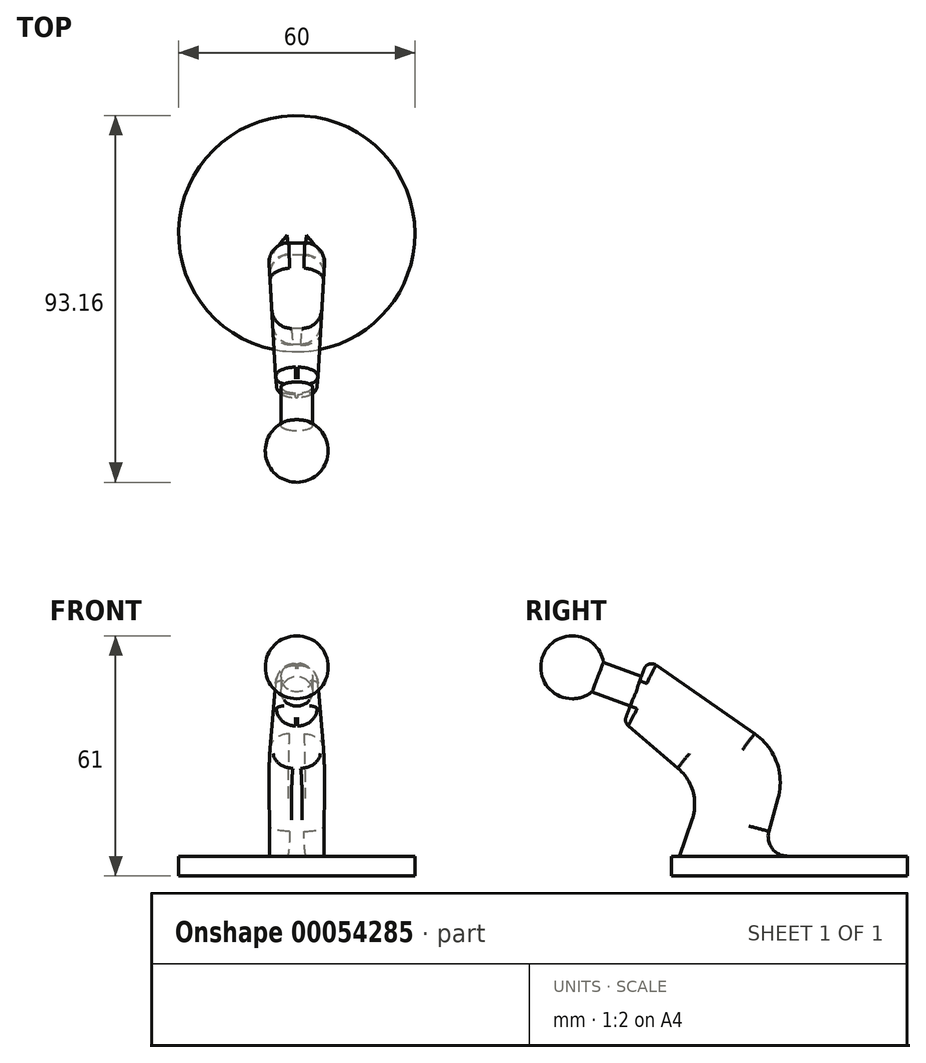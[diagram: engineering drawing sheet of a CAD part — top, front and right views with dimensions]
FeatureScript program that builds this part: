
annotation { "Feature Type Name" : "Feature", "Feature Type Description" : "" }
export const myFeature = defineFeature(function(context is Context, id is Id, definition is map)
    precondition{}
    {
        {
            var Q0;
            Q0=qCreatedBy(makeId("Top.planeOp"),FACE);
            var sketch = newSketch(context, id + "F0", { "sketchPlane" : qUnion([Q0])});
            skCircle(sketch, "E0", {"center": v(0, 0) * mm, "radius": 30 * mm});
            skSolve(sketch);
        }
        {
            var Q0;
            Q0 = qSketchRegion(id + "F0", true);
            extrude(context, id + "F1", {"entities" : qUnion([Q0]), "depth" : 5 * mm});
        }
        {
            var Q0;
            Q0=makeQuery(id+"F1.opExtrude","CAP_FACE",FACE,{"disambiguationData":[OSD([sQuery(id+"F0.wireOp",EDGE,"E0")])],"isStart":false});
            var sketch = newSketch(context, id + "F2", { "sketchPlane" : qUnion([Q0])});
            skLineSegment(sketch, "E1", {"start": v(-7.5, 0) * mm, "end": v(7.5, 0) * mm});
            skLineSegment(sketch, "E2", {"start": v(7.5, 0) * mm, "end": v(5, -42) * mm});
            skLineSegment(sketch, "E3", {"start": v(5, -42) * mm, "end": v(-5, -42) * mm});
            skLineSegment(sketch, "E4", {"start": v(-5, -42) * mm, "end": v(-7.5, 0) * mm});
            skSolve(sketch);
        }
        {
            var Q0;
            Q0 = qSketchRegion(id + "F2", true);
            extrude(context, id + "F3", {"entities" : qUnion([Q0]), "operationType" : NewBodyOperationType.ADD, "depth" : 50 * mm});
        }
        {
            var Q0;
            Q0=qCreatedBy(makeId("Right.planeOp"),FACE);
            var sketch = newSketch(context, id + "F4", { "sketchPlane" : qUnion([Q0])});
            skLineSegment(sketch, "E5", {"start": v(-7, 5) * mm, "end": v(0, 30) * mm});
            skLineSegment(sketch, "E6", {"start": v(0, 30) * mm, "end": v(-36, 55) * mm});
            skLineSegment(sketch, "E7", {"start": v(-36, 55) * mm, "end": v(-42, 39) * mm});
            skLineSegment(sketch, "E8", {"start": v(-42, 39) * mm, "end": v(-22, 22) * mm});
            skLineSegment(sketch, "E9", {"start": v(-22, 22) * mm, "end": v(-28, 5) * mm});
            skLineSegment(sketch, "E10", {"start": v(-28, 5) * mm, "end": v(-50, 5) * mm});
            skLineSegment(sketch, "E11", {"start": v(-50, 5) * mm, "end": v(-50, 60.74) * mm});
            skLineSegment(sketch, "E12", {"start": v(-50, 60.74) * mm, "end": v(11.13, 60.74) * mm});
            skLineSegment(sketch, "E13", {"start": v(11.13, 60.74) * mm, "end": v(11.13, 7.19) * mm});
            skLineSegment(sketch, "E14", {"start": v(11.13, 7.19) * mm, "end": v(0, 5) * mm});
            skLineSegment(sketch, "E15", {"start": v(0, 5) * mm, "end": v(-7, 5) * mm});
            skSolve(sketch);
        }
        {
            var Q0;
            Q0 = qSketchRegion(id + "F4", true);
            extrude(context, id + "F5", {"entities" : qUnion([Q0]), "operationType" : NewBodyOperationType.REMOVE, "endBound" : BoundingType.SYMMETRIC, "oppositeDirection" : true, "depth" : 25 * mm});
        }
        {
            var Q0;
            Q0=makeQuery(id+"F5.boolean.opBoolean","COPY",EDGE,{"derivedFrom":makeQuery(id+"F5.opExtrude","SWEPT_EDGE",EDGE,{"disambiguationData":[OSD([sQuery(id+"F4.wireOp",EDGE,"E5"),sQuery(id+"F4.wireOp",EDGE,"E6")])]})});
            fillet(context, id + "F6", {"entities" : qUnion([Q0]), "radius" : 15 * mm, "tangentPropagation" : true, "allowEdgeOverflow" : false});
        }
        {
            var Q0;
            Q0=makeQuery(id+"F5.boolean.opBoolean","COPY",EDGE,{"derivedFrom":makeQuery(id+"F5.opExtrude","SWEPT_EDGE",EDGE,{"disambiguationData":[OSD([sQuery(id+"F4.wireOp",EDGE,"E8"),sQuery(id+"F4.wireOp",EDGE,"E9")])]})});
            fillet(context, id + "F7", {"entities" : qUnion([Q0]), "radius" : 12 * mm, "tangentPropagation" : true, "allowEdgeOverflow" : false});
        }
        {
            var Q0;
            {var subQ0=sQuery(id+"F2.wireOp",EDGE,"E2");Q0=makeQuery(id+"F3.boolean.opBoolean","SPLIT",EDGE,{"disambiguationData":[topologyDisambiguationEdgeConnected([makeQuery(id+"F1.opExtrude","CAP_FACE",FACE,{"disambiguationData":[OSD([sQuery(id+"F0.wireOp",EDGE,"E0")])],"isStart":false})])],"derivedFrom":makeQuery(id+"F3.opExtrude","CAP_EDGE",EDGE,{"disambiguationData":[OSD([subQ0])],"isStart":true})});}
            var Q1;
            Q1=makeQuery(id+"F5.boolean.opBoolean","COPY",EDGE,{"derivedFrom":makeQuery(id+"F5.opExtrude","SWEPT_EDGE",EDGE,{"disambiguationData":[OSD([sQuery(id+"F4.wireOp",EDGE,"E5"),sQuery(id+"F4.wireOp",EDGE,"E15")])]})});
            var Q2;
            {var subQ0=sQuery(id+"F2.wireOp",EDGE,"E4");Q2=makeQuery(id+"F3.boolean.opBoolean","SPLIT",EDGE,{"disambiguationData":[topologyDisambiguationEdgeConnected([makeQuery(id+"F1.opExtrude","CAP_FACE",FACE,{"disambiguationData":[OSD([sQuery(id+"F0.wireOp",EDGE,"E0")])],"isStart":false})])],"derivedFrom":makeQuery(id+"F3.opExtrude","CAP_EDGE",EDGE,{"disambiguationData":[OSD([subQ0])],"isStart":true})});}
            fillet(context, id + "F8", {"entities" : qUnion([Q0, Q1, Q2]), "radius" : 5 * mm, "tangentPropagation" : true, "allowEdgeOverflow" : false});
        }
        {
            var Q0;
            Q0=makeQuery(id+"F5.boolean.opBoolean","INTERSECT",EDGE,{"derivedFrom":[makeQuery(id+"F3.opExtrude","SWEPT_FACE",FACE,{"disambiguationData":[OSD([sQuery(id+"F2.wireOp",EDGE,"E2")])]}),makeQuery(id+"F5.opExtrude","SWEPT_FACE",FACE,{"disambiguationData":[OSD([sQuery(id+"F4.wireOp",EDGE,"E7")])]})]});
            var Q1;
            Q1=makeQuery(id+"F5.boolean.opBoolean","COPY",EDGE,{"derivedFrom":makeQuery(id+"F5.opExtrude","SWEPT_EDGE",EDGE,{"disambiguationData":[OSD([sQuery(id+"F4.wireOp",EDGE,"E6"),sQuery(id+"F4.wireOp",EDGE,"E7")])]})});
            var Q2;
            Q2=makeQuery(id+"F5.boolean.opBoolean","COPY",EDGE,{"derivedFrom":makeQuery(id+"F5.opExtrude","SWEPT_EDGE",EDGE,{"disambiguationData":[OSD([sQuery(id+"F4.wireOp",EDGE,"E7"),sQuery(id+"F4.wireOp",EDGE,"E8")])]})});
            var Q3;
            Q3=makeQuery(id+"F5.boolean.opBoolean","INTERSECT",EDGE,{"derivedFrom":[makeQuery(id+"F3.opExtrude","SWEPT_FACE",FACE,{"disambiguationData":[OSD([sQuery(id+"F2.wireOp",EDGE,"E4")])]}),makeQuery(id+"F5.opExtrude","SWEPT_FACE",FACE,{"disambiguationData":[OSD([sQuery(id+"F4.wireOp",EDGE,"E7")])]})]});
            fillet(context, id + "F9", {"entities" : qUnion([Q0, Q1, Q2, Q3]), "radius" : 2 * mm, "tangentPropagation" : true, "allowEdgeOverflow" : false});
        }
        {
            var Q0;
            Q0=makeQuery(id+"F5.boolean.opBoolean","INTERSECT",EDGE,{"derivedFrom":[makeQuery(id+"F3.opExtrude","SWEPT_FACE",FACE,{"disambiguationData":[OSD([sQuery(id+"F2.wireOp",EDGE,"E2")])]}),makeQuery(id+"F5.opExtrude","SWEPT_FACE",FACE,{"disambiguationData":[OSD([sQuery(id+"F4.wireOp",EDGE,"E6")])]})]});
            var Q1;
            Q1=makeQuery(id+"F5.boolean.opBoolean","INTERSECT",EDGE,{"derivedFrom":[makeQuery(id+"F3.opExtrude","SWEPT_FACE",FACE,{"disambiguationData":[OSD([sQuery(id+"F2.wireOp",EDGE,"E4")])]}),makeQuery(id+"F5.opExtrude","SWEPT_FACE",FACE,{"disambiguationData":[OSD([sQuery(id+"F4.wireOp",EDGE,"E6")])]})]});
            var Q2;
            Q2=makeQuery(id+"F7.opFillet","BLEND_EDGE",EDGE,{"blendedFrom":[makeQuery(id+"F5.boolean.opBoolean","COPY",EDGE,{"derivedFrom":makeQuery(id+"F5.opExtrude","SWEPT_EDGE",EDGE,{"disambiguationData":[OSD([sQuery(id+"F4.wireOp",EDGE,"E8"),sQuery(id+"F4.wireOp",EDGE,"E9")])]})}),makeQuery(id+"F3.opExtrude","SWEPT_FACE",FACE,{"disambiguationData":[OSD([sQuery(id+"F2.wireOp",EDGE,"E2")])]})],"blendedInto":[makeQuery(id+"F3.opExtrude","SWEPT_FACE",FACE,{"disambiguationData":[OSD([sQuery(id+"F2.wireOp",EDGE,"E2")])]})]});
            var Q3;
            Q3=makeQuery(id+"F7.opFillet","BLEND_EDGE",EDGE,{"blendedFrom":[makeQuery(id+"F5.boolean.opBoolean","COPY",EDGE,{"derivedFrom":makeQuery(id+"F5.opExtrude","SWEPT_EDGE",EDGE,{"disambiguationData":[OSD([sQuery(id+"F4.wireOp",EDGE,"E8"),sQuery(id+"F4.wireOp",EDGE,"E9")])]})}),makeQuery(id+"F3.opExtrude","SWEPT_FACE",FACE,{"disambiguationData":[OSD([sQuery(id+"F2.wireOp",EDGE,"E4")])]})],"blendedInto":[makeQuery(id+"F3.opExtrude","SWEPT_FACE",FACE,{"disambiguationData":[OSD([sQuery(id+"F2.wireOp",EDGE,"E4")])]})]});
            fillet(context, id + "F10", {"entities" : qUnion([Q0, Q1, Q2, Q3]), "radius" : 5 * mm, "tangentPropagation" : true, "allowEdgeOverflow" : false});
        }
        {
            var Q0;
            Q0=makeQuery(id+"F5.boolean.opBoolean","COPY",FACE,{"derivedFrom":makeQuery(id+"F5.opExtrude","SWEPT_FACE",FACE,{"disambiguationData":[OSD([sQuery(id+"F4.wireOp",EDGE,"E7")])]})});
            var sketch = newSketch(context, id + "F11", { "sketchPlane" : qUnion([Q0])});
            skCircle(sketch, "E16", {"center": v(0, 30.18) * mm, "radius": 4 * mm});
            skSolve(sketch);
        }
        {
            var Q0;
            Q0 = qSketchRegion(id + "F11", true);
            extrude(context, id + "F12", {"entities" : qUnion([Q0]), "operationType" : NewBodyOperationType.ADD, "depth" : 12.24 * mm, "hasSecondDirection" : true, "secondDirectionOppositeDirection" : true, "secondDirectionDepth" : 1.23 * mm});
        }
        {
            var Q0;
            Q0=qCreatedBy(makeId("Right.planeOp"),FACE);
            var sketch = newSketch(context, id + "F13", { "sketchPlane" : qUnion([Q0])});
            skArc(sketch, "E17", {"start": v(-55.16, 45) * mm, "mid": v(-47.16, 53) * mm, "end": v(-55.16, 61) * mm});
            skLineSegment(sketch, "E18", {"start": v(-55.16, 53) * mm, "end": v(-55.16, 45) * mm});
            skLineSegment(sketch, "E19", {"start": v(-55.16, 53) * mm, "end": v(-55.16, 61) * mm});
            skSolve(sketch);
        }
        {
            var Q0;
            Q0=makeQuery(id+"F13.imprint","IMPRINT",FACE,{"disambiguationData":[TD([[makeQuery(id+"F13.imprint","IMPRINT",EDGE,{"derivedFrom":sQuery(id+"F13.wireOp",EDGE,"E17")}),1.0]])]});
            var Q1;
            Q1=sQuery(id+"F13.wireOp",EDGE,"E19");
            revolve(context, id + "F14", {"operationType" : NewBodyOperationType.ADD, "entities" : qUnion([Q0]), "axis" : qUnion([Q1]), "revolveType" : RevolveType.FULL});
        }
    });
